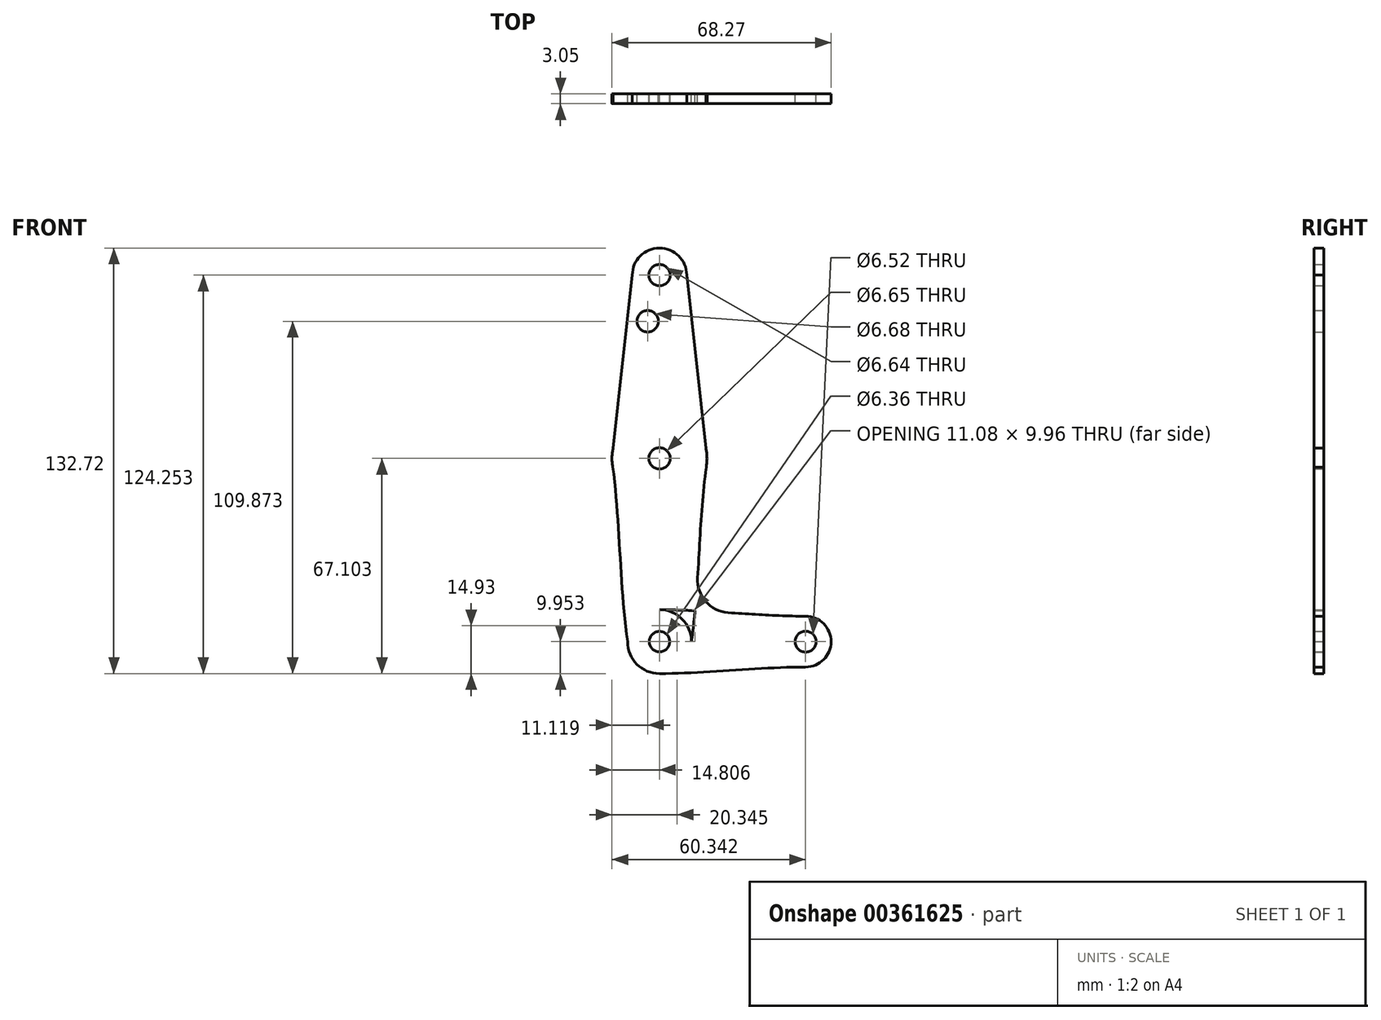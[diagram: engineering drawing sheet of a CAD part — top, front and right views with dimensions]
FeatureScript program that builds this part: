
annotation { "Feature Type Name" : "Feature", "Feature Type Description" : "" }
export const myFeature = defineFeature(function(context is Context, id is Id, definition is map)
    precondition{}
    {
        {
            var Q0;
            Q0=qCreatedBy(makeId("Front.planeOp"),FACE);
            var sketch = newSketch(context, id + "F0", { "sketchPlane" : qUnion([Q0])});
            skLineSegment(sketch, "E0", {"start": v(-40.37, 60.65) * mm, "end": v(-40.37, -53.65) * mm});
            skCircle(sketch, "E1", {"center": v(-40.37, 60.65) * mm, "radius": 8.47 * mm});
            skCircle(sketch, "E2", {"center": v(-40.37, 3.5) * mm, "radius": 14.8 * mm});
            skCircle(sketch, "E3", {"center": v(-40.37, -53.65) * mm, "radius": 9.96 * mm});
            skLineSegment(sketch, "E4", {"start": v(-40.37, -53.65) * mm, "end": v(5.16, -53.65) * mm});
            skCircle(sketch, "E5", {"center": v(5.16, -53.65) * mm, "radius": 7.93 * mm});
            skFitSpline(sketch, "E6", {"points": [v(-31.9, 60.65) * mm, v(-25.56, 3.5) * mm], "startDerivative": vector(6.34, -57.15) * mm, "endDerivative": vector(6.34, -57.15) * mm});
            skFitSpline(sketch, "E7", {"points": [v(-25.62, 2.2) * mm, v(-30.42, -53.65) * mm], "startDerivative": vector(-7.91, -55.65) * mm, "endDerivative": vector(-7.91, -55.65) * mm});
            skFitSpline(sketch, "E8", {"points": [v(-48.84, 60.65) * mm, v(-55.18, 3.5) * mm], "startDerivative": vector(-6.34, -57.15) * mm, "endDerivative": vector(-6.34, -57.15) * mm});
            skFitSpline(sketch, "E9", {"points": [v(-55.1, 2.03) * mm, v(-50.33, -53.65) * mm], "startDerivative": vector(7.91, -55.68) * mm, "endDerivative": vector(7.91, -55.68) * mm});
            skFitSpline(sketch, "E10", {"points": [v(5.16, -45.72) * mm, v(-40.37, -43.7) * mm], "startDerivative": vector(-44.43, 0) * mm, "endDerivative": vector(-44.43, 0) * mm});
            skFitSpline(sketch, "E11", {"points": [v(5.16, -61.58) * mm, v(-40.37, -63.6) * mm], "startDerivative": vector(-44.43, 0) * mm, "endDerivative": vector(-44.43, 0) * mm});
            skCircle(sketch, "E12", {"center": v(-40.37, 60.65) * mm, "radius": 3.32 * mm});
            skCircle(sketch, "E13", {"center": v(-44.06, 46.27) * mm, "radius": 3.34 * mm});
            skCircle(sketch, "E14", {"center": v(-40.37, -53.65) * mm, "radius": 3.18 * mm});
            skCircle(sketch, "E15", {"center": v(5.16, -53.65) * mm, "radius": 3.26 * mm});
            skCircle(sketch, "E16", {"center": v(-40.37, 3.5) * mm, "radius": 3.32 * mm});
            skArc(sketch, "E17.filletArc", {"start": v(-28.5, -33.75) * mm, "mid": v(-25.98, -41.15) * mm, "end": v(-18.97, -44.62) * mm});
            skSolve(sketch);
        }
        {
            var Q0;
            Q0 = qSketchRegion(id + "F0", true);
            var Q1;
            {var subQ0=sQuery(id+"F0.wireOp",EDGE,"E3");var subQ1=sQuery(id+"F0.wireOp",EDGE,"E0");var subQ2=makeQuery(id+"F0.imprint","INTERSECT",VERTEX,{"derivedFrom":[subQ1,subQ0]});Q1=makeQuery(id+"F0.imprint","IMPRINT",FACE,{"disambiguationData":[TD([[makeQuery(id+"F0.imprint","IMPRINT",EDGE,{"disambiguationData":[TD([[subQ2,-1.0]])],"derivedFrom":subQ1}),1.0]])]});}
            extrude(context, id + "F1", {"entities" : qUnion([Q0, Q1]), "depth" : 3.05 * mm});
        }
    });
